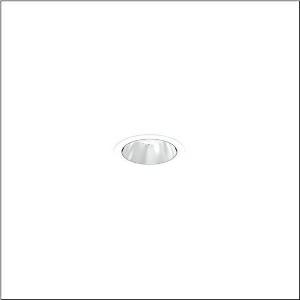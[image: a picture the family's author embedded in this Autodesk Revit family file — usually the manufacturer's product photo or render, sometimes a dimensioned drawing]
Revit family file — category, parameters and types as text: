
# Revit family: lunis_21_s_51db15ta91c
name_source: partatom
category: Lighting Fixtures
units: mm (PartAtom-declared; Revit-internal decimal feet)

## family parameters
Cut with Voids When Loaded = No
Host = Face
Light Source = No
Part Type = Normal
Room Calculation Point = No
Round Connector Dimension = Use Diameter
Shared = No

## types (1)
- --- (1 x LED 3000 K ... 6500 K, 1260 lm, 8 W, 4000K)
    Apparent Load = 8 VA
    CIE Flux Codes = 93 99 100 100 100
    Color Rendering = 80
    Color Temperature = 4000K
    Default Elevation = 1800 mm
    Description = Lunis 21 S, downlight, light control with lens, of PMMA, anti glare with reflector, of PC, highly specular, light emission: direct distribution, LED rated luminous flux: 1.260lm, light colour: 8tw, with terminal, 5-pole, mains connection: 220..240V, AC, 50..60Hz, housing, round, of diecast aluminium, traffic white (RAL 9016), diameter: 84mm, clamping range: 1..40mm, protection rating (complete): IP20, protection rating (on room side): IP54, insulation class (complete): insulation class II (safety insulation), certification: CE, impact resistance: IK03, packaging unit: 1 piece
    Height = 0 mm  [stored 0 ft]
    Lamp = 1 x LED 3000 K ... 6500 K
    Lamp Light Flux = 1260 lm
    Lamp Power = 8 W
    Lamp count = 1
    Length = 84 mm
    Luminous efficacy = 158 lm/W
    Manufacturer = Siteco
    ModVariant = No
    Model = 51DB15TA91C
    Mounting Place = Ceiling
    Mounting Type = Recessed
    Number of Poles = 1
    OnlyDefault = Yes
    Power Factor = 1
    Product Name = Lunis 21 S
    Product group = downlight
    ProductGroupID = 401
    Protection Class = Protection class II
    Protection Degree = IP 20
    RLX_Detail_Level = 1
    RLX_Emergency_Light_Flux = 0 lm
    RLX_Emergency_Type = 0
    RLX_Emergency_Type_DB = No
    RlxData = <blob elided: 8497 chars, md5=aac898d3>
    Socket = socket
    Standby Power = 0 W
    System Light Flux = 1260 lm
    System Power = 8 W
    Type Comments = individual setting: CCT=4000K, colour temperature 4000K, luminous flux: 100 % | (OFF | OFF | ON | OFF) | 200 mA
    Type Image = l_1290840.jpg
    URL = http://relux.com
    VarID = @adj_036581
    Voltage = 0 V
    Weight = 0.00 kg
    Width = 0 mm  [stored 0 ft]

note: [stored X ft] marks values corroborated as IEEE doubles in the binary element streams (Revit-internal decimal feet)

## geometry (parser evidence)
native form markers: Sweep x8
no freeform markers — native parametric forms only
